FCSTD DOCUMENT  (FreeCAD 1.0R39319 (Git))
Label: chainSawSword
License: All rights reserved
LicenseURL: https://en.wikipedia.org/wiki/All_rights_reserved
objects: Spreadsheet::Sheet×1, Sketcher::SketchObject×1, PartDesign::Body×1
note: 3 computed .brp shape members not serialized (recipe doc carries the construction recipe); baked Part::Feature solids carry a one-line shape summary decoded from their .brp

FEATURE [Spreadsheet::Sheet] Spreadsheet001  label="Dimensions"
  cells = A1='total_length; B1=1000; A2='handle_length; B2=150; A3='handle_diameter; B3=35; A4='crossguard_length; B4=120; A5='crossguard_width; B5=25; A6='crossguard_thickness; B6=12; A7='blade_length; B7=650; A8='blade_width; B8=90; A9='blade_thickness; B9=25; A10='guide_width; B10=12; A11='guide_depth; B11=6; A12='tooth_length; B12=25; A13='tooth_height; B13=20; A14='tooth_width; B14=6; A15='tooth_spacing; B15=45; A16='motor_housing_length; B16=60; A17='motor_housing_width; B17=40; A18='motor_housing_depth; B18=30; A19='sprocket_diameter; B19=50; A20='sprocket_thickness; B20=12; A21='trigger_length; B21=60; A22='trigger_travel; B22=8
FEATURE [Sketcher::SketchObject] Sketch
  ArcFitTolerance = 1e-06
  AttachmentSupport = -> [XY_Plane]
  FullyConstrained = false
  MakeInternals = false
  MapMode = 5
  sketch-geometry (4):
    g0: LineSegment StartX=0 StartY=0 StartZ=0 EndX=100.1 EndY=0 EndZ=0
    g1: LineSegment StartX=100.1 StartY=0 StartZ=0 EndX=100.1 EndY=23.3249 EndZ=0
    g2: LineSegment StartX=100.1 StartY=23.3249 StartZ=0 EndX=0 EndY=23.3249 EndZ=0
    g3: LineSegment StartX=0 StartY=23.3249 StartZ=0 EndX=0 EndY=0 EndZ=0
  constraints (9):
    c: Coincident(g0,g1)
    c: Coincident(g1,g2)
    c: Coincident(g2,g3)
    c: Coincident(g3,g0)
    c: Horizontal(g0)
    c: Horizontal(g2)
    c: Vertical(g1)
    c: Vertical(g3)
    c: Coincident(g0,g-1)
FEATURE [PartDesign::Body] Body
  AllowCompound = false
  Group = -> [Sketch]
  Origin = -> Origin
